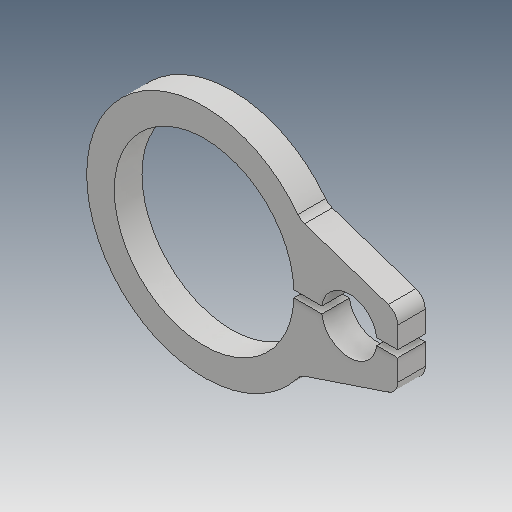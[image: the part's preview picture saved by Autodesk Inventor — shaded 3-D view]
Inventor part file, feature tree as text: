
AUTODESK INVENTOR PART (.ipt)
format: ipt  version: 2018 (Build 220112000, 112)  size: 109,056 bytes
history: native  units: mm
features: fillet x1
ambient origin geometry x8: Origin, YZ Plane, XZ Plane, XY Plane, X Axis, Y Axis, Z Axis, Center Point
bodies: Volumenkörper1 (feature_tree)
feature tree (1):
  fillet  "Fillet1"  [1 undecoded]
note: 1 required parameter value undecoded (feature->parameter linkage not recoverable at this tier; creation-order binding heuristic only, values carry confidence <= 0.55)
